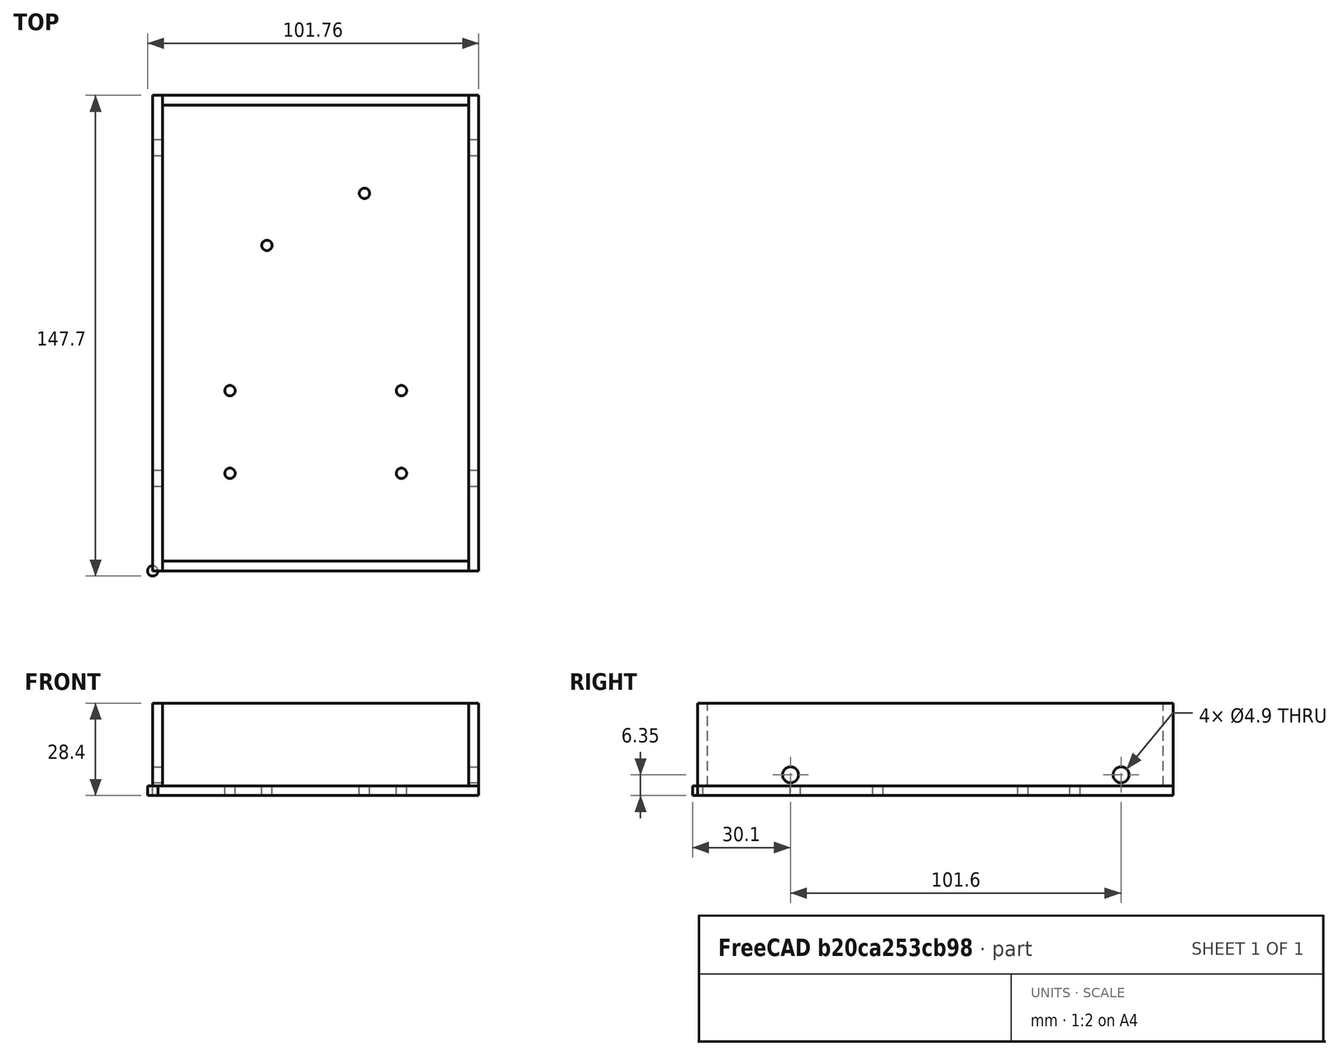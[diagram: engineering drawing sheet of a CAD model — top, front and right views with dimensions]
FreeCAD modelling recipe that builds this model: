
FCSTD DOCUMENT  (FreeCAD 0.19R24267 +148 (Git))
Label: 3_5_inchDiskSized
License: All rights reserved
LicenseURL: http://en.wikipedia.org/wiki/All_rights_reserved
objects: Part::Box×5, Part::Cylinder×3, Part::FeaturePython×3, Part::Compound×3, Part::Cut×2
note: 13 computed .brp shape members not serialized (recipe doc carries the construction recipe); baked Part::Feature solids carry a one-line shape summary decoded from their .brp
EXTERNAL_REF file=globals.FCStd obj=Spreadsheet

FEATURE [Part::Box] Box  label="bottom"
  AttacherType = Attacher::AttachEngine3D
  Height = 3
  Length = 100.16
  Width = 146.1
  expr: Height = <<globals>>#<<globals>>.faceplateSizeZ
FEATURE [Part::Box] Box001  label="sideA"
  AttacherType = Attacher::AttachEngine3D
  Height = 25.4
  Length = 3
  Placement = pos=(0,0,3) rot=(0,0,1;0rad)
  Width = 146.1
  expr: Height = <<front>>.Height
  expr: .Placement.Base.z = <<bottom>>.Height
  expr: Width = <<bottom>>.Width
  expr: Length = <<globals>>#<<globals>>.faceplateSizeZ
FEATURE [Part::Box] Box002  label="sideB"
  AttacherType = Attacher::AttachEngine3D
  Height = 25.4
  Length = 3
  Placement = pos=(97.16,0,3) rot=(0,0,1;0rad)
  Width = 146.1
  expr: Height = <<front>>.Height
  expr: .Placement.Base.x = <<bottom>>.Length - Length
  expr: Length = <<globals>>#<<globals>>.faceplateSizeZ
  expr: Width = <<bottom>>.Width
  expr: .Placement.Base.z = <<bottom>>.Height
FEATURE [Part::Box] Box003  label="front"
  AttacherType = Attacher::AttachEngine3D
  Height = 25.4
  Length = 94.16
  Placement = pos=(3,0,3) rot=(0,0,1;0rad)
  Width = 3
  expr: .Placement.Base.z = Width
  expr: .Placement.Base.x = Width
  expr: Length = <<bottom>>.Length - <<globals>>#<<globals>>.faceplateSizeZ * 2mm
  expr: Width = <<globals>>#<<globals>>.faceplateSizeZ
FEATURE [Part::Box] Box004  label="back"
  AttacherType = Attacher::AttachEngine3D
  Height = 25.4
  Length = 94.16
  Placement = pos=(3,143.1,3) rot=(0,0,1;0rad)
  Width = 3
  expr: Height = <<front>>.Height
  expr: .Placement.Base.y = <<bottom>>.Width - Width
  expr: Width = <<globals>>#<<globals>>.faceplateSizeZ
  expr: Length = <<bottom>>.Length - <<globals>>#<<globals>>.faceplateSizeZ * 2mm
  expr: .Placement.Base.x = Width
  expr: .Placement.Base.z = Width
FEATURE [Part::Cylinder] Cylinder  label="holeA"
  Angle = 360
  AttacherType = Attacher::AttachEngine3D
  Height = 3
  Placement = pos=(0,28.5,6.35) rot=(0,1,0;1.5708rad)
  Radius = 2.45
  expr: Radius = <<globals>>#<<globals>>.rivetNutRadius
  expr: Height = <<globals>>#<<globals>>.faceplateSizeZ
FEATURE [Part::FeaturePython] Array  label="mountingHoles"  # Draft array (typed FeaturePython)
  Angle = 360
  ArrayType = 0
  Axis = (0,0,1)
  Base = -> Cylinder
  Center = (0,0,0)
  Count = 4
  ExpandArray = false
  Fuse = false
  IntervalAxis = (0,0,0)
  IntervalX = (97.16,0,0)
  IntervalY = (0,101.6,0)
  IntervalZ = (0,0,100)
  NumberCircles = 3
  NumberPolar = 5
  NumberX = 2
  NumberY = 2
  NumberZ = 1
  PlacementList = 4 placements: [(0,28.5,6.35),(0,130.1,6.35),(97.16,28.5,6.35),(97.16,130.1,6.35)]
  RadialDistance = 50
  ScaleList = (4) [(1,1,1),(1,1,1),(1,1,1),(1,1,1)]
  Symmetry = 1
  TangentialDistance = 25
  expr: .IntervalX.x = <<bottom>>.Length - <<holeA>>.Height
FEATURE [Part::Cylinder] Cylinder001  label="cheapbmcMountHoleA"
  Angle = 360
  AttacherType = Attacher::AttachEngine3D
  Height = 3
  Radius = 1.6
  expr: Height = <<globals>>#<<globals>>.faceplateSizeZ
FEATURE [Part::FeaturePython] Array001  label="cheapBMCMountingHoles"  # Draft array (typed FeaturePython)
  Angle = 360
  ArrayType = 0
  Axis = (0,0,1)
  Base = -> Cylinder001
  Center = (0,0,0)
  Count = 4
  ExpandArray = false
  Fuse = false
  IntervalAxis = (0,0,0)
  IntervalX = (52.7,0,0)
  IntervalY = (0,25.4,0)
  IntervalZ = (0,0,100)
  NumberCircles = 3
  NumberPolar = 5
  NumberX = 2
  NumberY = 2
  NumberZ = 1
  Placement = pos=(23.73,30,0) rot=(0,0,1;0rad)
  PlacementList = 4 placements: [(0,0,0),(0,25.4,0),(52.7,0,0),(52.7,25.4,0)]
  RadialDistance = 50
  ScaleList = (4) [(1,1,1),(1,1,1),(1,1,1),(1,1,1)]
  Symmetry = 1
  TangentialDistance = 25
  expr: .Placement.Base.x = <<bottom>>.Length / 2 - .IntervalX.x / 2
FEATURE [Part::Cylinder] Cylinder002  label="PSUMountA"
  Angle = 360
  AttacherType = Attacher::AttachEngine3D
  Height = 3
  Radius = 1.6
  expr: Height = <<globals>>#<<globals>>.faceplateSizeZ
FEATURE [Part::FeaturePython] Array002  label="PSUHoles"  # Draft array (typed FeaturePython)
  Angle = 360
  ArrayType = 0
  Axis = (0,0,1)
  Base = -> Cylinder002
  Center = (0,0,0)
  Count = 2
  ExpandArray = false
  Fuse = false
  IntervalAxis = (0,0,0)
  IntervalX = (30,16,0)
  IntervalY = (0,100,0)
  IntervalZ = (0,0,100)
  NumberCircles = 3
  NumberPolar = 5
  NumberX = 2
  NumberY = 1
  NumberZ = 1
  Placement = pos=(35.08,100,0) rot=(0,0,1;0rad)
  PlacementList = 2 placements: [(0,0,0),(30,16,0)]
  RadialDistance = 50
  ScaleList = (2) [(1,1,1),(1,1,1)]
  Symmetry = 1
  TangentialDistance = 25
  expr: .Placement.Base.x = <<bottom>>.Length / 2 - .IntervalX.x / 2
FEATURE [Part::Compound] Compound001  label="holes"
  Links = -> [Array001,Array002]
FEATURE [Part::Cut] Cut  label="bottomWithHoles"
  Base = -> Box
  Tool = -> Compound001
FEATURE [Part::Compound] Compound002  label="sides"
  Links = -> [Box001,Box002]
FEATURE [Part::Cut] Cut001  label="sidesWithHoles"
  Base = -> Compound002
  Tool = -> Array
FEATURE [Part::Compound] Compound  label="case"
  Links = -> [Box004,Box003,Cut,Cut001]
